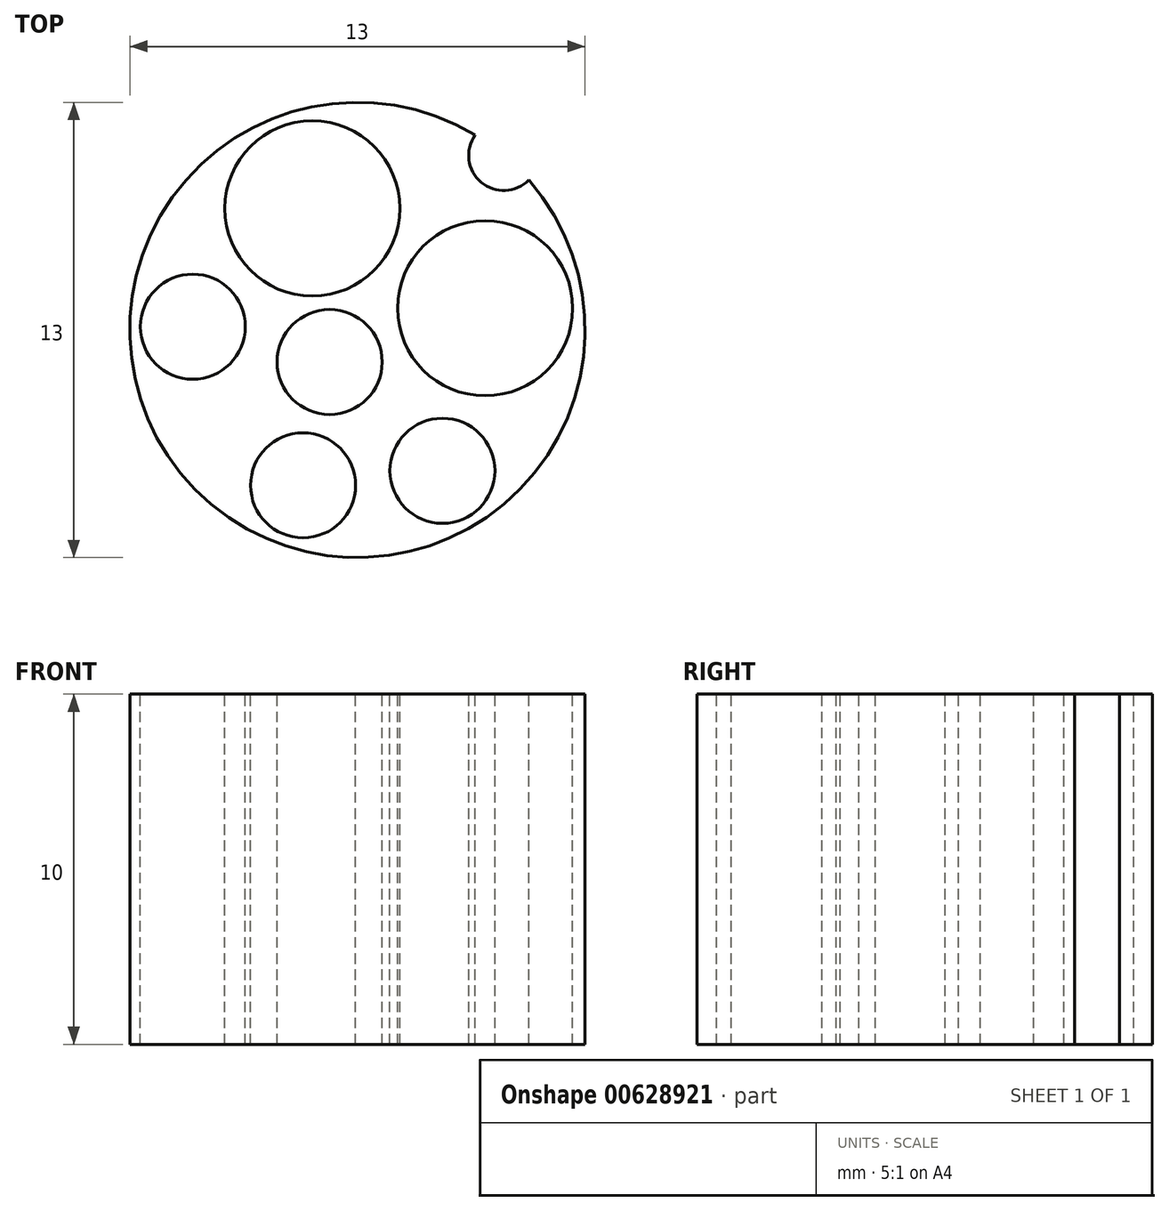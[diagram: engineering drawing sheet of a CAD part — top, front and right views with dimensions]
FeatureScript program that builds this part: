
annotation { "Feature Type Name" : "Feature", "Feature Type Description" : "" }
export const myFeature = defineFeature(function(context is Context, id is Id, definition is map)
    precondition{}
    {
        {
            var Q0;
            Q0=qCreatedBy(makeId("Top.planeOp"),FACE);
            var sketch = newSketch(context, id + "F0", { "sketchPlane" : qUnion([Q0])});
            skCircle(sketch, "E0", {"center": v(0, 0) * mm, "radius": 6.5 * mm});
            skCircle(sketch, "E1", {"center": v(0, 0) * mm, "radius": 7.5 * mm});
            skSolve(sketch);
        }
        {
            var Q0;
            Q0=makeQuery(id+"F0.imprint","IMPRINT",FACE,{"disambiguationData":[TD([[makeQuery(id+"F0.imprint","IMPRINT",EDGE,{"derivedFrom":sQuery(id+"F0.wireOp",EDGE,"E0")}),1.0]])]});
            extrude(context, id + "F1", {"entities" : qUnion([Q0]), "depth" : 10 * mm, "offsetDistance" : 25 * mm});
        }
        {
            var Q0;
            Q0=makeQuery(id+"F1.opExtrude","CAP_FACE",FACE,{"disambiguationData":[OSD([sQuery(id+"F0.wireOp",EDGE,"E0")])],"isStart":false});
            cPlane(context, id + "F2", {"entities" : qUnion([Q0]), "cplaneType" : CPlaneType.OFFSET, "offset" : 0 * mm, "width" : 150 * mm, "height" : 150 * mm});
        }
        {
            var Q0;
            Q0=qCreatedBy(id+"F2.planeOp",FACE);
            var sketch = newSketch(context, id + "F3", { "sketchPlane" : qUnion([Q0])});
            skLineSegment(sketch, "E2", {"start": v(0, 0) * mm, "end": v(12.27, 2.08) * mm, "construction": true});
            skLineSegment(sketch, "E3", {"start": v(-3.9, 10.48) * mm, "end": v(0, 0) * mm, "construction": true});
            skLineSegment(sketch, "E4", {"start": v(0, 0) * mm, "end": v(-4.15, -11.9) * mm, "construction": true});
            skLineSegment(sketch, "E5", {"start": v(0, 0) * mm, "end": v(9.36, -15.52) * mm, "construction": true});
            skCircle(sketch, "E6", {"center": v(-1.29, 3.47) * mm, "radius": 2.5 * mm});
            skCircle(sketch, "E7", {"center": v(3.65, 0.62) * mm, "radius": 2.5 * mm});
            skCircle(sketch, "E8", {"center": v(0, 0) * mm, "radius": 4.7 * mm, "construction": true});
            skCircle(sketch, "E9", {"center": v(2.43, -4.02) * mm, "radius": 1.5 * mm});
            skCircle(sketch, "E10", {"center": v(-4.7, 0.1) * mm, "radius": 1.5 * mm});
            skLineSegment(sketch, "E11", {"start": v(0, 0) * mm, "end": v(11.63, 13.87) * mm, "construction": true});
            skCircle(sketch, "E12", {"center": v(4.18, 4.98) * mm, "radius": 1 * mm});
            skLineSegment(sketch, "E13", {"start": v(0, 0) * mm, "end": v(-12.8, -14.8) * mm, "construction": true});
            skCircle(sketch, "E14", {"center": v(-0.8, -0.92) * mm, "radius": 1.5 * mm});
            skCircle(sketch, "E15", {"center": v(-1.55, -4.44) * mm, "radius": 1.5 * mm});
            skCircle(sketch, "E16", {"center": v(0, 0) * mm, "radius": 6.5 * mm, "construction": true});
            skCircle(sketch, "E17", {"center": v(0, 0) * mm, "radius": 3.7 * mm, "construction": true});
            skLineSegment(sketch, "E18.0", {"start": v(6.5, 3.75) * mm, "end": v(6.5, -3.75) * mm, "construction": true});
            skLineSegment(sketch, "E18.1", {"start": v(6.5, -3.75) * mm, "end": v(0, -7.5) * mm, "construction": true});
            skLineSegment(sketch, "E18.2", {"start": v(0, -7.5) * mm, "end": v(-6.5, -3.75) * mm, "construction": true});
            skLineSegment(sketch, "E18.3", {"start": v(-6.5, -3.75) * mm, "end": v(-6.5, 3.75) * mm, "construction": true});
            skLineSegment(sketch, "E18.4", {"start": v(-6.5, 3.75) * mm, "end": v(0, 7.5) * mm, "construction": true});
            skLineSegment(sketch, "E18.5", {"start": v(0, 7.5) * mm, "end": v(6.5, 3.75) * mm, "construction": true});
            skPoint(sketch, "E18.0.midPoint", {"position": v(6.5, 0) * mm});
            skSolve(sketch);
        }
        {
            var Q0;
            Q0=makeQuery(id+"F3.imprint","IMPRINT",FACE,{"disambiguationData":[TD([[makeQuery(id+"F3.imprint","IMPRINT",EDGE,{"derivedFrom":sQuery(id+"F3.wireOp",EDGE,"E6")}),1.0]])]});
            var Q1;
            Q1=makeQuery(id+"F3.imprint","IMPRINT",FACE,{"disambiguationData":[TD([[makeQuery(id+"F3.imprint","IMPRINT",EDGE,{"derivedFrom":sQuery(id+"F3.wireOp",EDGE,"E10")}),1.0]])]});
            var Q2;
            Q2=makeQuery(id+"F3.imprint","IMPRINT",FACE,{"disambiguationData":[TD([[makeQuery(id+"F3.imprint","IMPRINT",EDGE,{"derivedFrom":sQuery(id+"F3.wireOp",EDGE,"E14")}),1.0]])]});
            var Q3;
            Q3=makeQuery(id+"F3.imprint","IMPRINT",FACE,{"disambiguationData":[TD([[makeQuery(id+"F3.imprint","IMPRINT",EDGE,{"derivedFrom":sQuery(id+"F3.wireOp",EDGE,"E12")}),1.0]])]});
            var Q4;
            Q4=makeQuery(id+"F3.imprint","IMPRINT",FACE,{"disambiguationData":[TD([[makeQuery(id+"F3.imprint","IMPRINT",EDGE,{"derivedFrom":sQuery(id+"F3.wireOp",EDGE,"E7")}),1.0]])]});
            var Q5;
            Q5=makeQuery(id+"F3.imprint","IMPRINT",FACE,{"disambiguationData":[TD([[makeQuery(id+"F3.imprint","IMPRINT",EDGE,{"derivedFrom":sQuery(id+"F3.wireOp",EDGE,"E9")}),1.0]])]});
            var Q6;
            Q6=makeQuery(id+"F3.imprint","IMPRINT",FACE,{"disambiguationData":[TD([[makeQuery(id+"F3.imprint","IMPRINT",EDGE,{"derivedFrom":sQuery(id+"F3.wireOp",EDGE,"E15")}),1.0]])]});
            extrude(context, id + "F4", {"entities" : qUnion([Q0, Q1, Q2, Q3, Q4, Q5, Q6]), "operationType" : NewBodyOperationType.REMOVE, "endBound" : BoundingType.SYMMETRIC, "oppositeDirection" : true, "depth" : 50 * mm, "offsetDistance" : 25 * mm});
        }
        {
            var Q0;
            Q0=makeQuery(id+"F3.imprint","IMPRINT",FACE,{"disambiguationData":[TD([[makeQuery(id+"F3.imprint","IMPRINT",EDGE,{"derivedFrom":sQuery(id+"F3.wireOp",EDGE,"E12")}),1.0]])]});
            extrude(context, id + "F5", {"entities" : qUnion([Q0]), "operationType" : NewBodyOperationType.REMOVE, "endBound" : BoundingType.SYMMETRIC, "oppositeDirection" : true, "depth" : 30 * mm, "offsetDistance" : 25 * mm});
        }
    });
